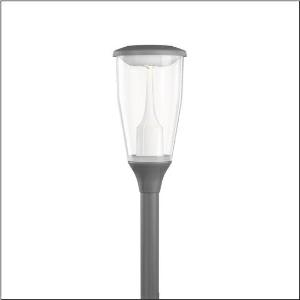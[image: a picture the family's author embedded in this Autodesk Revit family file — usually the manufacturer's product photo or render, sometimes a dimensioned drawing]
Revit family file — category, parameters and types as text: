
# Revit family: dl_11_iq___p1_0a_5xa5575bf14hp00022_48d3
name_source: partatom
category: Lighting Fixtures
units: mm (PartAtom-declared; Revit-internal decimal feet)

## family parameters
Cut with Voids When Loaded = No
Host = Face
Light Source = No
Part Type = Normal
Room Calculation Point = No
Round Connector Dimension = Use Diameter
Shared = No

## types (1)
- --- (1 x LED, 3950 lm, 33.6 W, 2200K)
    Apparent Load = 34 VA
    CIE Flux Codes = 33 63 91 94 100
    Color Rendering = 70
    Color Temperature = 2200K
    Default Elevation = 1800 mm
    Description = DL 11 iQ, mast luminaire, Module 540 iQ-SR, primary light control with 3 zone facetted reflector, of plastic, silver coated, highly specular, structured, primary optical cover: cover, of PMMA, transparent, light distribution: P1.0a, light emission: direct distribution, primary light characteristic: asymmetric, installation type: post-top, LED, High Power LED, light colour: 722, colour temperature: 2200K, control: Street-Remote, Auto-Match, Temp-Guard, Lumen-Switch, Night-Set, Smart-Wire, Light-Fading, Desk-Remote (wireless, voltage-free reading and setting of iQ features in the workshop via application-optimized NFC function/RFID function), optimised constant luminous flux control (CLO 2.0), mains connection: 220..240V, AC, 50/60Hz, connection cable pre-assembled, cable length: 5,5m, wiring characteristics: H07RN-F, 5-core, 1.5mm², start of lifetime: 34W, end of service life: 36W, luminaire housing, upper part, of diecast aluminium, coated, Siteco® metallic grey (DB 702S), spigot size: 76mm (post-top), post-top mast mounting element, of diecast aluminium, coated, Siteco® metallic grey (DB 702S), Module 540 iQ-SR, traffic white (RAL 9016), equipment: Power, protection rating (complete): IP66, insulation class (complete): insulation class II (safety insulation), certification: CE, ENEC, ENEC+, VDE, packaging unit: 1 piece

Light Distribution: P1.0a
    Height = 665 mm
    Lamp = 1 x LED
    Lamp Light Flux = 3950 lm
    Lamp Power = 33.6 W
    Lamp count = 1
    Length = 334 mm
    Luminous efficacy = 118 lm/W
    Manufacturer = Siteco
    ModVariant = No
    Model = 5XA5575BF14HP00022
    Number of Poles = 1
    OnlyDefault = Yes
    Power Factor = 1
    Product Name = DL 11 iQ | P1.0a
    Product group = mast luminaire | pylon top
    ProductGroupID = 6100
    Protection Class = Protection class II
    Protection Degree = IP 66
    RLX_Detail_Level = 1
    RLX_Emergency_Light_Flux = 0 lm
    RLX_Emergency_Type = 0
    RLX_Emergency_Type_DB = No
    RlxData = <blob elided: 104977 chars, md5=d2765121>
    Socket = socket
    Standby Power = 0 W
    System Light Flux = 3950 lm
    System Power = 34 W
    Type Comments = factory setting: luminous flux: 100 % | dim-lin: 254 | 695 mA
    Type Image = l_1258354.jpg
    URL = http://relux.com
    VarID = @adj_001699
    Voltage = 0 V
    Weight = 0.00 kg
    Width = 0 mm  [stored 0 ft]

note: [stored X ft] marks values corroborated as IEEE doubles in the binary element streams (Revit-internal decimal feet)

## geometry (parser evidence)
native form markers: Blend x4, Sweep x10
no freeform markers — native parametric forms only
